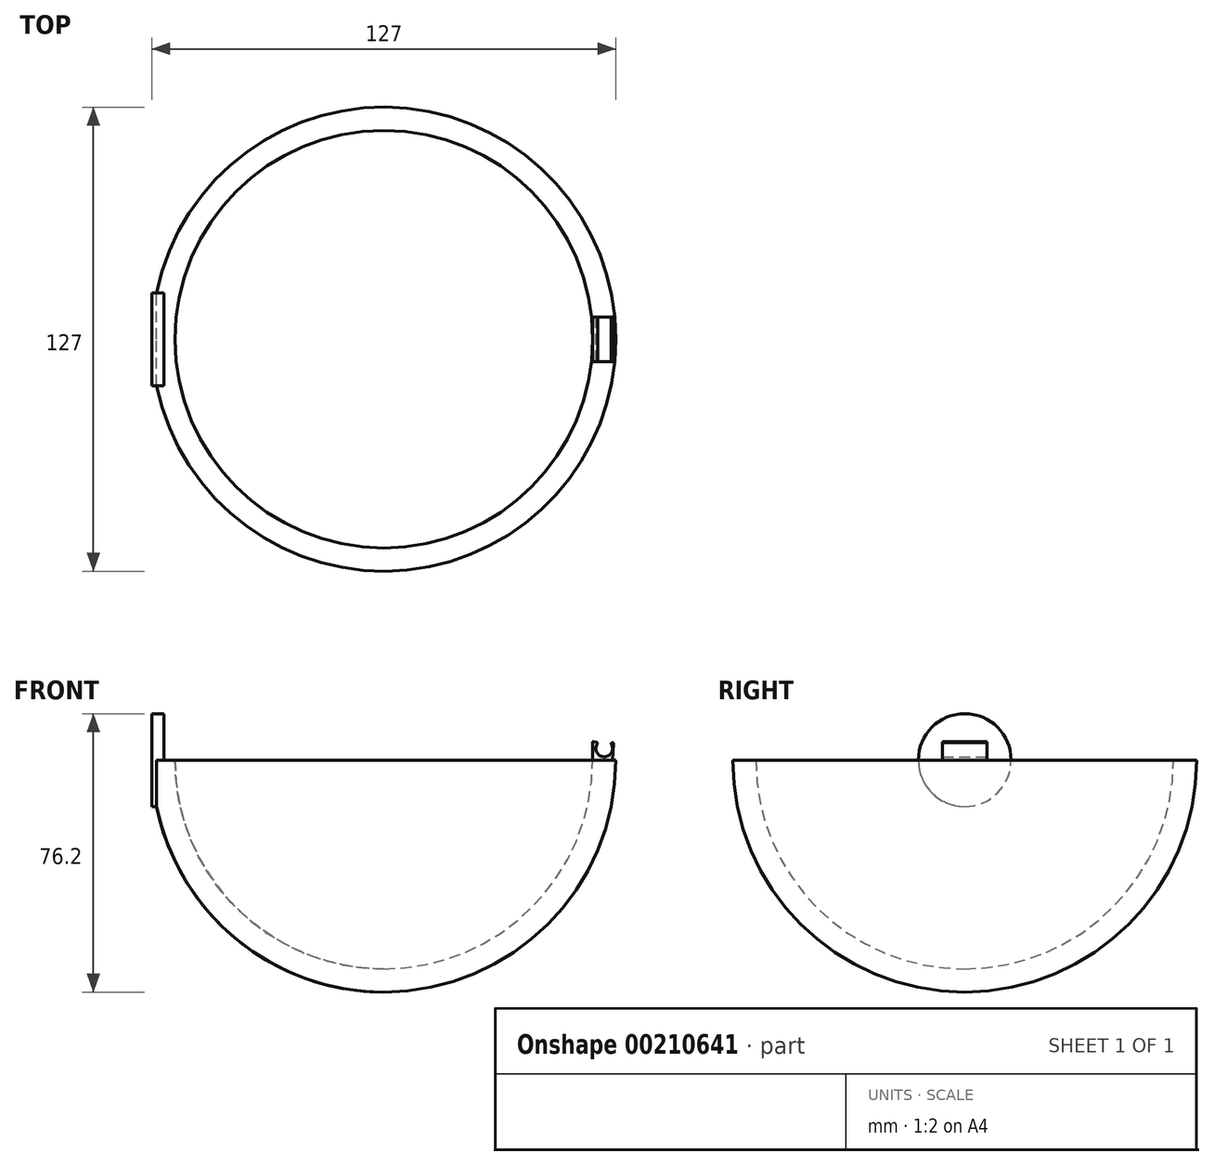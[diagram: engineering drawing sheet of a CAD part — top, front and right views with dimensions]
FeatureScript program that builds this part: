
annotation { "Feature Type Name" : "Feature", "Feature Type Description" : "" }
export const myFeature = defineFeature(function(context is Context, id is Id, definition is map)
    precondition{}
    {
        {
            var Q0;
            Q0=qCreatedBy(makeId("Front.planeOp"),FACE);
            var sketch = newSketch(context, id + "F0", { "sketchPlane" : qUnion([Q0])});
            skLineSegment(sketch, "E0", {"start": v(-63.5, 0) * mm, "end": v(-57.15, 0) * mm});
            skLineSegment(sketch, "E1.MirrorCS", {"start": v(0, -57.15) * mm, "end": v(0, -63.5) * mm});
            skArc(sketch, "E2.MirrorCS", {"start": v(0, -57.15) * mm, "mid": v(-40.41, -40.41) * mm, "end": v(-57.15, 0) * mm});
            skArc(sketch, "E3.MirrorCS", {"start": v(0, -63.5) * mm, "mid": v(-44.9, -44.9) * mm, "end": v(-63.5, 0) * mm});
            skPoint(sketch, "E4.end.orphan", {"position": v(0, 63.5) * mm});
            skPoint(sketch, "E4.start.orphan", {"position": v(0, 57.15) * mm});
            skSolve(sketch);
        }
        {
            var Q0;
            Q0=makeQuery(id+"F0.imprint","IMPRINT",FACE,{"disambiguationData":[TD([[makeQuery(id+"F0.imprint","IMPRINT",EDGE,{"derivedFrom":sQuery(id+"F0.wireOp",EDGE,"E0")}),-1.0]])]});
            var Q1;
            Q1=sQuery(id+"F0.wireOp",EDGE,"E1.MirrorCS");
            revolve(context, id + "F1", {"entities" : qUnion([Q0]), "axis" : qUnion([Q1]), "revolveType" : RevolveType.FULL});
        }
        {
            var Q0;
            Q0=qCreatedBy(makeId("Front.planeOp"),FACE);
            var sketch = newSketch(context, id + "F2", { "sketchPlane" : qUnion([Q0])});
            skArc(sketch, "E5", {"start": v(-63.5, 0) * mm, "mid": v(0, -63.5) * mm, "end": v(63.5, 0) * mm});
            skLineSegment(sketch, "E6", {"start": v(63.5, 0) * mm, "end": v(57.15, 0) * mm});
            skArc(sketch, "E7", {"start": v(58.44, 4.46) * mm, "mid": v(60.25, 0.9) * mm, "end": v(62.3, 4.34) * mm});
            skLineSegment(sketch, "E8", {"start": v(57.15, 0) * mm, "end": v(57.15, 4.84) * mm});
            skLineSegment(sketch, "E9", {"start": v(57.47, 5.08) * mm, "end": v(58.3, 4.85) * mm});
            skLineSegment(sketch, "E10", {"start": v(62.46, 4.71) * mm, "end": v(62.58, 4.74) * mm});
            skLineSegment(sketch, "E11", {"start": v(62.89, 4.47) * mm, "end": v(62.57, 0) * mm});
            skPoint(sketch, "E12.visualSharp", {"position": v(57.15, 5.17) * mm});
            skArc(sketch, "E12.filletArc", {"start": v(57.47, 5.08) * mm, "mid": v(57.25, 5.04) * mm, "end": v(57.15, 4.84) * mm});
            skPoint(sketch, "E13.visualSharp", {"position": v(62.9, 4.8) * mm});
            skArc(sketch, "E13.filletArc", {"start": v(62.89, 4.47) * mm, "mid": v(62.8, 4.68) * mm, "end": v(62.58, 4.74) * mm});
            skPoint(sketch, "E14.visualSharp", {"position": v(62.08, 4.64) * mm});
            skArc(sketch, "E14.filletArc", {"start": v(62.46, 4.71) * mm, "mid": v(62.28, 4.57) * mm, "end": v(62.3, 4.34) * mm});
            skPoint(sketch, "E15.visualSharp", {"position": v(58.66, 4.74) * mm});
            skArc(sketch, "E15.filletArc", {"start": v(58.44, 4.46) * mm, "mid": v(58.46, 4.7) * mm, "end": v(58.3, 4.85) * mm});
            skSolve(sketch);
        }
        {
            var Q0;
            Q0=makeQuery(id+"F2.imprint","IMPRINT",FACE,{"disambiguationData":[TD([[makeQuery(id+"F2.imprint","IMPRINT",EDGE,{"derivedFrom":sQuery(id+"F2.wireOp",EDGE,"E7")}),-1.0]])]});
            extrude(context, id + "F3", {"entities" : qUnion([Q0]), "operationType" : NewBodyOperationType.ADD, "endBound" : BoundingType.SYMMETRIC, "depth" : 12.2 * mm});
        }
        {
            var Q0;
            Q0=qCreatedBy(makeId("Right.planeOp"),FACE);
            cPlane(context, id + "F4", {"entities" : qUnion([Q0]), "cplaneType" : CPlaneType.OFFSET, "offset" : 63.5 * mm, "oppositeDirection" : true, "width" : 152.4 * mm, "height" : 152.4 * mm});
        }
        {
            var Q0;
            Q0=qCreatedBy(id+"F4.planeOp",FACE);
            var sketch = newSketch(context, id + "F5", { "sketchPlane" : qUnion([Q0])});
            skCircle(sketch, "E16", {"center": v(0, 0) * mm, "radius": 12.7 * mm});
            skSolve(sketch);
        }
        {
            var Q0;
            Q0=makeQuery(id+"F5.imprint","IMPRINT",FACE,{"disambiguationData":[TD([[makeQuery(id+"F5.imprint","IMPRINT",EDGE,{"derivedFrom":sQuery(id+"F5.wireOp",EDGE,"E16")}),1.0]])]});
            extrude(context, id + "F6", {"entities" : qUnion([Q0]), "operationType" : NewBodyOperationType.ADD, "depth" : 3.3 * mm});
        }
    });
